# Revit family: Edelstahlrohrschelle V2A, ohne AG, ohne VS, Ø321-410
name_source: partatom
category: HLS-Bauteile
revit_build: Autodesk Revit 2017 (Build: 20190507_1515(x64)
units: mm (PartAtom-declared; Revit-internal decimal feet)

## family parameters
Arbeitsebenenbasiert = Ja
Beim Laden mit Abzugskörper schneiden = Nein
Bemaßung runder Anschluss = Durchmesser verwenden
Gemeinsam genutzt = Ja
Immer vertikal = Nein
Raumberechnungspunkt = Nein
Teiletyp = Normal

## types (4) — shared parameters
A = 5 mm  [stored 0.0164042 ft]
Anschluss = ohne Anschluss
Bauart = zweiteilig
DF1 = 32 mm  [stored 0.104987 ft]
DF2 = 37 mm  [stored 0.121391 ft]
DVS = 17 mm
Fabrikat = MEFA
Firma = MEFA Befestigungs- und Montagesysteme GmbH
Kurztext1 = Rohrschelle Edelstahl V2A 50x5,0
MB = 50 mm  [stored 0.164042 ft]
MD = 5 mm  [stored 0.0164042 ft]
Material = Edelstahl
Materialmaße = 50x5,0 mm
Mengeneinheit = St
Rohraußendurchmesser Zoll = Zoll
Verschluss = Schraubenverschluss
Vorgabe-Ansicht = 1219 mm
max. zul. Last horizontal = 0.00 kN
max. zul. Last vertikal = 0.00 kN
vpe = 1 St
zero-valued in all types: HGA, Nennweite DN Rohr, Rohraußendurchmesser, Stärke Material

## per-type parameters (varying)
| type | AB | Achsabstand | Artikelnummer | B | D | Dmax | Dmin | EAN | Gewicht | Gewicht pro Bauteil | H | Kurztext2 | R | RM | S | max. Rohraußendurchmesser | min. Rohraußendurchmesser |
| Edelstahlrohrschelle V2A, o.AG, o.VS, Ø321-325 | 4 mm  [stored 0.0131234 ft] | 372 mm | 0465046 | 404 mm | 325 mm  [stored 1.06627 ft] | 325 mm  [stored 1.06627 ft] | 321 mm  [stored 1.05315 ft] | 4250928411655 | 2.10 kg | 2.10 kg | 335 mm | 321 - 325 mm ohne Anschluss | 163 mm | 168 mm | 372 mm  [stored 1.22047 ft] | 325 mm  [stored 1.06627 ft] | 321 mm  [stored 1.05315 ft] |
| Edelstahlrohrschelle V2A, o.AG, o.VS, Ø356-360 | 4 mm  [stored 0.0131234 ft] | 407 mm | 0465051 | 439 mm | 360 mm  [stored 1.1811 ft] | 360 mm  [stored 1.1811 ft] | 356 mm  [stored 1.16798 ft] | 4250928411662 | 2.30 kg | 2.30 kg | 370 mm  [stored 1.21391 ft] | 356 - 360 mm ohne Anschluss | 180 mm  [stored 0.590551 ft] | 185 mm  [stored 0.606955 ft] | 407 mm  [stored 1.3353 ft] | 360 mm  [stored 1.1811 ft] | 356 mm  [stored 1.16798 ft] |
| Edelstahlrohrschelle V2A, o.AG, o.VS, Ø361-370 | 9 mm | 416 mm | 0465052 | 449 mm  [stored 1.4731 ft] | 370 mm  [stored 1.21391 ft] | 370 mm  [stored 1.21391 ft] | 361 mm  [stored 1.18438 ft] | 4250928411679 | 2.33 kg | 2.33 kg | 380 mm | 361 - 370 mm ohne Anschluss | 185 mm  [stored 0.606955 ft] | 190 mm  [stored 0.62336 ft] | 417 mm  [stored 1.36811 ft] | 370 mm  [stored 1.21391 ft] | 361 mm  [stored 1.18438 ft] |
| Edelstahlrohrschelle V2A, o.AG, o.VS, Ø401-410 | 9 mm | 456 mm | 0465056 | 489 mm | 410 mm  [stored 1.34514 ft] | 410 mm  [stored 1.34514 ft] | 401 mm  [stored 1.31562 ft] | 4250928411686 | 2.56 kg | 2.56 kg | 420 mm  [stored 1.37795 ft] | 401 - 410 mm ohne Anschluss | 205 mm  [stored 0.672572 ft] | 210 mm  [stored 0.688976 ft] | 457 mm  [stored 1.49934 ft] | 410 mm  [stored 1.34514 ft] | 401 mm  [stored 1.31562 ft] |

note: [stored X ft] marks values corroborated as IEEE doubles in the binary element streams (Revit-internal decimal feet)
